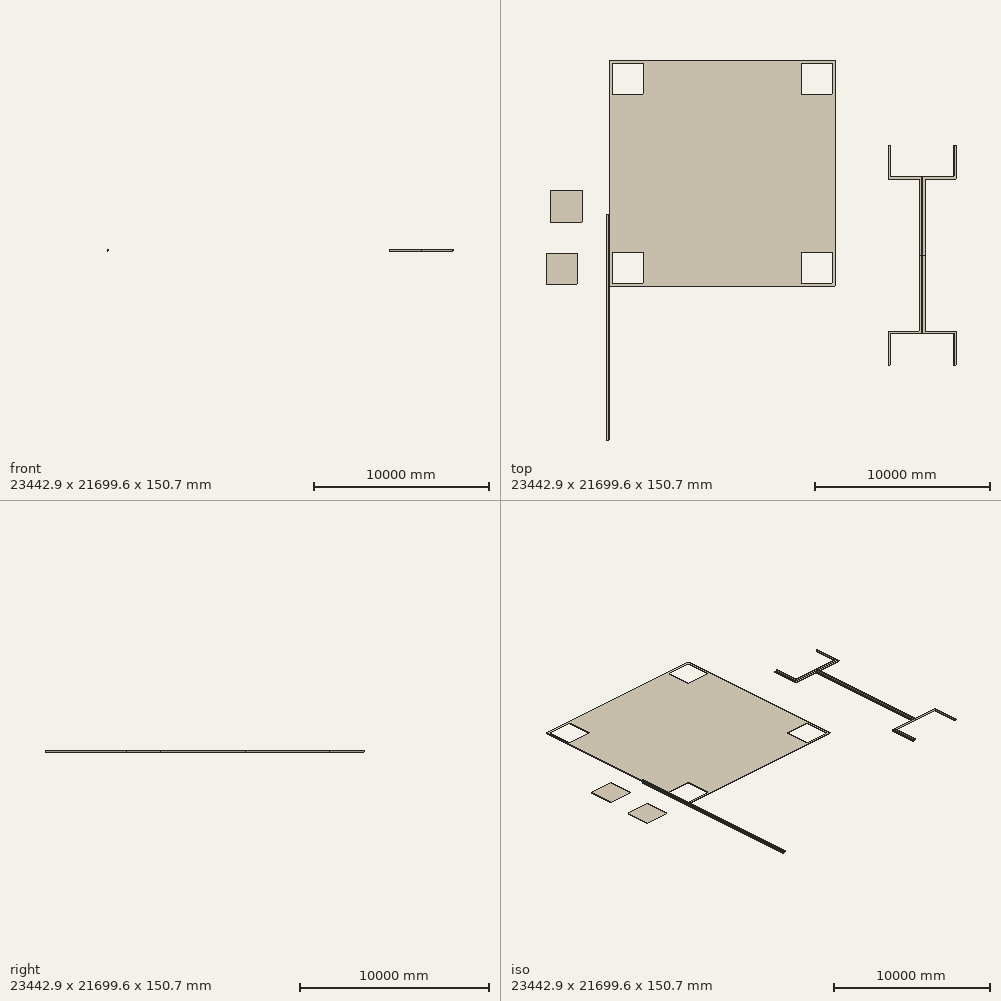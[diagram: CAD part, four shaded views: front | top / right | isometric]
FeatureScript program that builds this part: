
annotation { "Feature Type Name" : "Feature", "Feature Type Description" : "" }
export const myFeature = defineFeature(function(context is Context, id is Id, definition is map)
    precondition{}
    {
        {
            var Q0;
            Q0=qCreatedBy(makeId("Top.planeOp"),FACE);
            var sketch = newSketch(context, id + "F0", { "sketchPlane" : qUnion([Q0])});
            skLineSegment(sketch, "E0.bottom", {"start": v(-5778.74, -4100.38) * mm, "end": v(7121.26, -4100.38) * mm});
            skLineSegment(sketch, "E0.top", {"start": v(-5778.74, 8799.62) * mm, "end": v(7121.26, 8799.62) * mm});
            skLineSegment(sketch, "E0.left", {"start": v(-5778.74, -4100.38) * mm, "end": v(-5778.74, 8799.62) * mm});
            skLineSegment(sketch, "E0.right", {"start": v(7121.26, -4100.38) * mm, "end": v(7121.26, 8799.62) * mm});
            skLineSegment(sketch, "E1.bottom", {"start": v(-5628.74, 8649.62) * mm, "end": v(-3828.74, 8649.62) * mm});
            skLineSegment(sketch, "E1.top", {"start": v(-5628.74, 6849.62) * mm, "end": v(-3828.74, 6849.62) * mm});
            skLineSegment(sketch, "E1.left", {"start": v(-5628.74, 8649.62) * mm, "end": v(-5628.74, 6849.62) * mm});
            skLineSegment(sketch, "E1.right", {"start": v(-3828.74, 8649.62) * mm, "end": v(-3828.74, 6849.62) * mm});
            skLineSegment(sketch, "E2.bottom", {"start": v(-5628.74, -2150.38) * mm, "end": v(-3828.74, -2150.38) * mm});
            skLineSegment(sketch, "E2.top", {"start": v(-5628.74, -3950.38) * mm, "end": v(-3828.74, -3950.38) * mm});
            skLineSegment(sketch, "E2.left", {"start": v(-5628.74, -2150.38) * mm, "end": v(-5628.74, -3950.38) * mm});
            skLineSegment(sketch, "E2.right", {"start": v(-3828.74, -2150.38) * mm, "end": v(-3828.74, -3950.38) * mm});
            skLineSegment(sketch, "E3.bottom", {"start": v(5171.26, -2150.38) * mm, "end": v(6971.26, -2150.38) * mm});
            skLineSegment(sketch, "E3.top", {"start": v(5171.26, -3950.38) * mm, "end": v(6971.26, -3950.38) * mm});
            skLineSegment(sketch, "E3.left", {"start": v(5171.26, -2150.38) * mm, "end": v(5171.26, -3950.38) * mm});
            skLineSegment(sketch, "E3.right", {"start": v(6971.26, -2150.38) * mm, "end": v(6971.26, -3950.38) * mm});
            skLineSegment(sketch, "E4.bottom", {"start": v(5171.26, 8649.62) * mm, "end": v(6971.26, 8649.62) * mm});
            skLineSegment(sketch, "E4.top", {"start": v(5171.26, 6849.62) * mm, "end": v(6971.26, 6849.62) * mm});
            skLineSegment(sketch, "E4.left", {"start": v(5171.26, 8649.62) * mm, "end": v(5171.26, 6849.62) * mm});
            skLineSegment(sketch, "E4.right", {"start": v(6971.26, 8649.62) * mm, "end": v(6971.26, 6849.62) * mm});
            skSolve(sketch);
        }
        {
            var Q0;
            Q0=makeQuery(id+"F0.imprint","IMPRINT",FACE,{"disambiguationData":[TD([[makeQuery(id+"F0.imprint","IMPRINT",EDGE,{"derivedFrom":sQuery(id+"F0.wireOp",EDGE,"E0.bottom")}),1.0]])]});
            extrude(context, id + "F1", {"entities" : qUnion([Q0]), "depth" : 12 * mm, "offsetDistance" : 25 * mm});
        }
        {
            var Q0;
            Q0=qCreatedBy(makeId("Top.planeOp"),FACE);
            var sketch = newSketch(context, id + "F2", { "sketchPlane" : qUnion([Q0])});
            skLineSegment(sketch, "E5.bottom", {"start": v(-9395.46, -2196.4) * mm, "end": v(-7595.46, -2196.4) * mm});
            skLineSegment(sketch, "E5.top", {"start": v(-9395.46, -3996.4) * mm, "end": v(-7595.46, -3996.4) * mm});
            skLineSegment(sketch, "E5.left", {"start": v(-9395.46, -2196.4) * mm, "end": v(-9395.46, -3996.4) * mm});
            skLineSegment(sketch, "E5.right", {"start": v(-7595.46, -2196.4) * mm, "end": v(-7595.46, -3996.4) * mm});
            skSolve(sketch);
        }
        {
            var Q0;
            Q0 = qSketchRegion(id + "F2", true);
            extrude(context, id + "F3", {"entities" : qUnion([Q0]), "depth" : 12 * mm, "offsetDistance" : 25 * mm});
        }
        {
            var Q0;
            Q0=qCreatedBy(makeId("Top.planeOp"),FACE);
            var sketch = newSketch(context, id + "F4", { "sketchPlane" : qUnion([Q0])});
            skLineSegment(sketch, "E6.bottom", {"start": v(-9150.06, 1356.2) * mm, "end": v(-7350.06, 1356.2) * mm});
            skLineSegment(sketch, "E6.top", {"start": v(-9150.06, -443.8) * mm, "end": v(-7350.06, -443.8) * mm});
            skLineSegment(sketch, "E6.left", {"start": v(-9150.06, 1356.2) * mm, "end": v(-9150.06, -443.8) * mm});
            skLineSegment(sketch, "E6.right", {"start": v(-7350.06, 1356.2) * mm, "end": v(-7350.06, -443.8) * mm});
            skSolve(sketch);
        }
        {
            var Q0;
            Q0 = qSketchRegion(id + "F4", true);
            extrude(context, id + "F5", {"entities" : qUnion([Q0]), "depth" : 12 * mm, "offsetDistance" : 25 * mm});
        }
        {
            var Q0;
            Q0=qCreatedBy(makeId("Front.planeOp"),FACE);
            var sketch = newSketch(context, id + "F6", { "sketchPlane" : qUnion([Q0])});
            skLineSegment(sketch, "E7", {"start": v(-5951, 0.74) * mm, "end": v(-5801, 0.74) * mm});
            skLineSegment(sketch, "E8", {"start": v(-5801, 0.74) * mm, "end": v(-5801, 150.74) * mm});
            skLineSegment(sketch, "E9", {"start": v(-5801, 150.74) * mm, "end": v(-5825, 150.74) * mm});
            skLineSegment(sketch, "E10", {"start": v(-5825, 150.74) * mm, "end": v(-5825, 24.74) * mm});
            skLineSegment(sketch, "E11", {"start": v(-5825, 24.74) * mm, "end": v(-5951, 24.74) * mm});
            skLineSegment(sketch, "E12", {"start": v(-5951, 24.74) * mm, "end": v(-5951, 0.74) * mm});
            skSolve(sketch);
        }
        {
            var Q0;
            Q0 = qSketchRegion(id + "F6", true);
            extrude(context, id + "F7", {"entities" : qUnion([Q0]), "depth" : 12900 * mm, "offsetDistance" : 25 * mm});
        }
        {
            var Q0;
            Q0 = qSketchRegion(id + "F6", true);
            extrude(context, id + "F8", {"entities" : qUnion([Q0]), "depth" : 12900 * mm, "offsetDistance" : 25 * mm});
        }
        {
            var Q0;
            Q0=qCreatedBy(makeId("Top.planeOp"),FACE);
            var sketch = newSketch(context, id + "F9", { "sketchPlane" : qUnion([Q0])});
            skLineSegment(sketch, "E13", {"start": v(10297.45, 3978.85) * mm, "end": v(10297.45, 2178.85) * mm});
            skLineSegment(sketch, "E14", {"start": v(10297.45, 2178.85) * mm, "end": v(12097.45, 2178.85) * mm});
            skLineSegment(sketch, "E15", {"start": v(12097.45, 2178.85) * mm, "end": v(12097.45, -2321.15) * mm});
            skLineSegment(sketch, "E16", {"start": v(12097.45, -2321.15) * mm, "end": v(11947.45, -2321.15) * mm});
            skLineSegment(sketch, "E17", {"start": v(11947.45, -2321.15) * mm, "end": v(11947.45, 2028.85) * mm});
            skLineSegment(sketch, "E18", {"start": v(11947.45, 2028.85) * mm, "end": v(10147.45, 2028.85) * mm});
            skLineSegment(sketch, "E19", {"start": v(10147.45, 2028.85) * mm, "end": v(10147.45, 3978.85) * mm});
            skLineSegment(sketch, "E20", {"start": v(10147.45, 3978.85) * mm, "end": v(10297.45, 3978.85) * mm});
            skSolve(sketch);
        }
        {
            var Q0;
            Q0 = qSketchRegion(id + "F9", true);
            extrude(context, id + "F10", {"entities" : qUnion([Q0]), "depth" : 24 * mm, "offsetDistance" : 25 * mm});
        }
        {
            var Q0;
            Q0=makeQuery(id+"F10.opExtrude","CAP_FACE",FACE,{"disambiguationData":[OSD([sQuery(id+"F9.wireOp",EDGE,"E13"),sQuery(id+"F9.wireOp",EDGE,"E14"),sQuery(id+"F9.wireOp",EDGE,"E15"),sQuery(id+"F9.wireOp",EDGE,"E16"),sQuery(id+"F9.wireOp",EDGE,"E17"),sQuery(id+"F9.wireOp",EDGE,"E18"),sQuery(id+"F9.wireOp",EDGE,"E19"),sQuery(id+"F9.wireOp",EDGE,"E20")])],"isStart":false});
            var sketch = newSketch(context, id + "F11", { "sketchPlane" : qUnion([Q0])});
            skLineSegment(sketch, "E21", {"start": v(10297.45, 3978.85) * mm, "end": v(10273.45, 3978.85) * mm});
            skLineSegment(sketch, "E22", {"start": v(10273.45, 3978.85) * mm, "end": v(10273.45, 2154.85) * mm});
            skLineSegment(sketch, "E23", {"start": v(10273.45, 2154.85) * mm, "end": v(12073.45, 2154.85) * mm});
            skLineSegment(sketch, "E24", {"start": v(12073.45, 2154.85) * mm, "end": v(12073.45, -2321.15) * mm});
            skLineSegment(sketch, "E25", {"start": v(12073.45, -2321.15) * mm, "end": v(12097.45, -2321.15) * mm});
            skLineSegment(sketch, "E26", {"start": v(12097.45, -2321.15) * mm, "end": v(12097.45, 2178.85) * mm});
            skLineSegment(sketch, "E27", {"start": v(12097.45, 2178.85) * mm, "end": v(10297.45, 2178.85) * mm});
            skLineSegment(sketch, "E28", {"start": v(10297.45, 2178.85) * mm, "end": v(10297.45, 3978.85) * mm});
            skLineSegment(sketch, "E29", {"start": v(10273.45, 3978.85) * mm, "end": v(10297.45, 3978.85) * mm});
            skSolve(sketch);
        }
        {
            var Q0;
            Q0 = qSketchRegion(id + "F11", true);
            extrude(context, id + "F12", {"entities" : qUnion([Q0]), "operationType" : NewBodyOperationType.ADD, "depth" : 126 * mm, "offsetDistance" : 25 * mm});
        }
        {
            var Q0;
            Q0=makeQuery(id+"F10.opExtrude","SWEPT_BODY",BODY,{"disambiguationData":[OSD([sQuery(id+"F9.wireOp",EDGE,"E13"),sQuery(id+"F9.wireOp",EDGE,"E14"),sQuery(id+"F9.wireOp",EDGE,"E15"),sQuery(id+"F9.wireOp",EDGE,"E16"),sQuery(id+"F9.wireOp",EDGE,"E17"),sQuery(id+"F9.wireOp",EDGE,"E18"),sQuery(id+"F9.wireOp",EDGE,"E19"),sQuery(id+"F9.wireOp",EDGE,"E20")])]});
            var Q1;
            Q1=makeQuery(id+"F12.boolean.opBoolean","MERGE",FACE,{"derivedFrom":[makeQuery(id+"F10.opExtrude","SWEPT_FACE",FACE,{"disambiguationData":[OSD([sQuery(id+"F9.wireOp",EDGE,"E16")])]}),makeQuery(id+"F12.opExtrude","SWEPT_FACE",FACE,{"disambiguationData":[OSD([sQuery(id+"F11.wireOp",EDGE,"E25")])]})]});
            mirror(context, id + "F13", {"entities" : qUnion([Q0]), "mirrorPlane" : qUnion([Q1])});
        }
        {
            var Q0;
            Q0=makeQuery(id+"F13.opPattern","COPY",BODY,{"derivedFrom":makeQuery(id+"F10.opExtrude","SWEPT_BODY",BODY,{"disambiguationData":[OSD([sQuery(id+"F9.wireOp",EDGE,"E13"),sQuery(id+"F9.wireOp",EDGE,"E14"),sQuery(id+"F9.wireOp",EDGE,"E15"),sQuery(id+"F9.wireOp",EDGE,"E16"),sQuery(id+"F9.wireOp",EDGE,"E17"),sQuery(id+"F9.wireOp",EDGE,"E18"),sQuery(id+"F9.wireOp",EDGE,"E19"),sQuery(id+"F9.wireOp",EDGE,"E20")])]}),"instanceName":"1"});
            var Q1;
            Q1=makeQuery(id+"F10.opExtrude","SWEPT_BODY",BODY,{"disambiguationData":[OSD([sQuery(id+"F9.wireOp",EDGE,"E13"),sQuery(id+"F9.wireOp",EDGE,"E14"),sQuery(id+"F9.wireOp",EDGE,"E15"),sQuery(id+"F9.wireOp",EDGE,"E16"),sQuery(id+"F9.wireOp",EDGE,"E17"),sQuery(id+"F9.wireOp",EDGE,"E18"),sQuery(id+"F9.wireOp",EDGE,"E19"),sQuery(id+"F9.wireOp",EDGE,"E20")])]});
            var Q2;
            Q2=makeQuery(id+"F12.boolean.opBoolean","MERGE",FACE,{"derivedFrom":[makeQuery(id+"F10.opExtrude","SWEPT_FACE",FACE,{"disambiguationData":[OSD([sQuery(id+"F9.wireOp",EDGE,"E15")])]}),makeQuery(id+"F12.opExtrude","SWEPT_FACE",FACE,{"disambiguationData":[OSD([sQuery(id+"F11.wireOp",EDGE,"E26")])]})]});
            mirror(context, id + "F14", {"entities" : qUnion([Q0, Q1]), "mirrorPlane" : qUnion([Q2])});
        }
    });
